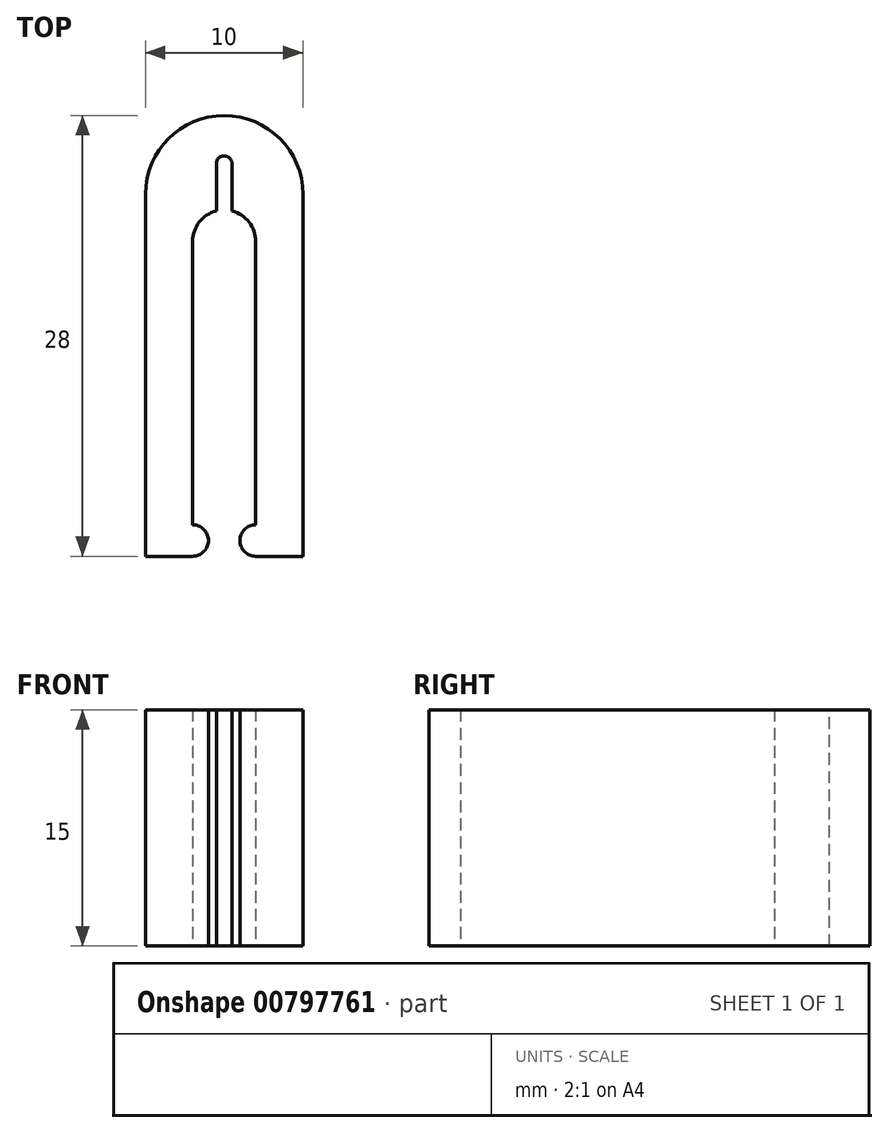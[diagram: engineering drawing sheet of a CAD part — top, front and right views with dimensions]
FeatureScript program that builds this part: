
annotation { "Feature Type Name" : "Feature", "Feature Type Description" : "" }
export const myFeature = defineFeature(function(context is Context, id is Id, definition is map)
    precondition{}
    {
        {
            var Q0;
            Q0=qCreatedBy(makeId("Top.planeOp"),FACE);
            var sketch = newSketch(context, id + "F0", { "sketchPlane" : qUnion([Q0])});
            skLineSegment(sketch, "E0", {"start": v(-2, -12.24) * mm, "end": v(-5, -12.24) * mm});
            skLineSegment(sketch, "E1", {"start": v(-5, -12.24) * mm, "end": v(-5, 10.76) * mm});
            skLineSegment(sketch, "E2", {"start": v(5, 10.76) * mm, "end": v(5, -12.24) * mm});
            skLineSegment(sketch, "E3", {"start": v(5, -12.24) * mm, "end": v(2, -12.24) * mm});
            skArc(sketch, "E4", {"start": v(5, 10.76) * mm, "mid": v(0, 15.76) * mm, "end": v(-5, 10.76) * mm});
            skArc(sketch, "E5", {"start": v(2, 7.76) * mm, "mid": v(0, 9.76) * mm, "end": v(-2, 7.76) * mm});
            skLineSegment(sketch, "E6", {"start": v(-2, 7.76) * mm, "end": v(-2, -10.24) * mm});
            skLineSegment(sketch, "E7", {"start": v(2, 7.76) * mm, "end": v(2, -10.24) * mm});
            skArc(sketch, "E8", {"start": v(-2, -12.24) * mm, "mid": v(-1, -11.24) * mm, "end": v(-2, -10.24) * mm});
            skArc(sketch, "E9", {"start": v(2, -10.24) * mm, "mid": v(1, -11.24) * mm, "end": v(2, -12.24) * mm});
            skLineSegment(sketch, "E10.bottom", {"start": v(-0.5, 9.7) * mm, "end": v(0.5, 9.7) * mm});
            skLineSegment(sketch, "E10.top", {"start": v(-0.5, 13.2) * mm, "end": v(0.5, 13.2) * mm});
            skLineSegment(sketch, "E10.left", {"start": v(-0.5, 9.7) * mm, "end": v(-0.5, 13.2) * mm});
            skLineSegment(sketch, "E10.right", {"start": v(0.5, 9.7) * mm, "end": v(0.5, 13.2) * mm});
            skSolve(sketch);
        }
        {
            var Q0;
            Q0=makeQuery(id+"F0.imprint","IMPRINT",FACE,{"disambiguationData":[TD([[makeQuery(id+"F0.imprint","IMPRINT",EDGE,{"derivedFrom":sQuery(id+"F0.wireOp",EDGE,"E0")}),-1.0]])]});
            extrude(context, id + "F1", {"entities" : qUnion([Q0]), "depth" : 15 * mm, "offsetDistance" : 25 * mm});
        }
        {
            var Q0;
            Q0=makeQuery(id+"F1.opExtrude","SWEPT_EDGE",EDGE,{"disambiguationData":[OSD([sQuery(id+"F0.wireOp",EDGE,"E10.top"),sQuery(id+"F0.wireOp",EDGE,"E10.left")])]});
            var Q1;
            Q1=makeQuery(id+"F1.opExtrude","SWEPT_EDGE",EDGE,{"disambiguationData":[OSD([sQuery(id+"F0.wireOp",EDGE,"E10.top"),sQuery(id+"F0.wireOp",EDGE,"E10.right")])]});
            fillet(context, id + "F2", {"entities" : qUnion([Q0, Q1]), "radius" : 0.5 * mm, "tangentPropagation" : true, "allowEdgeOverflow" : false});
        }
    });
